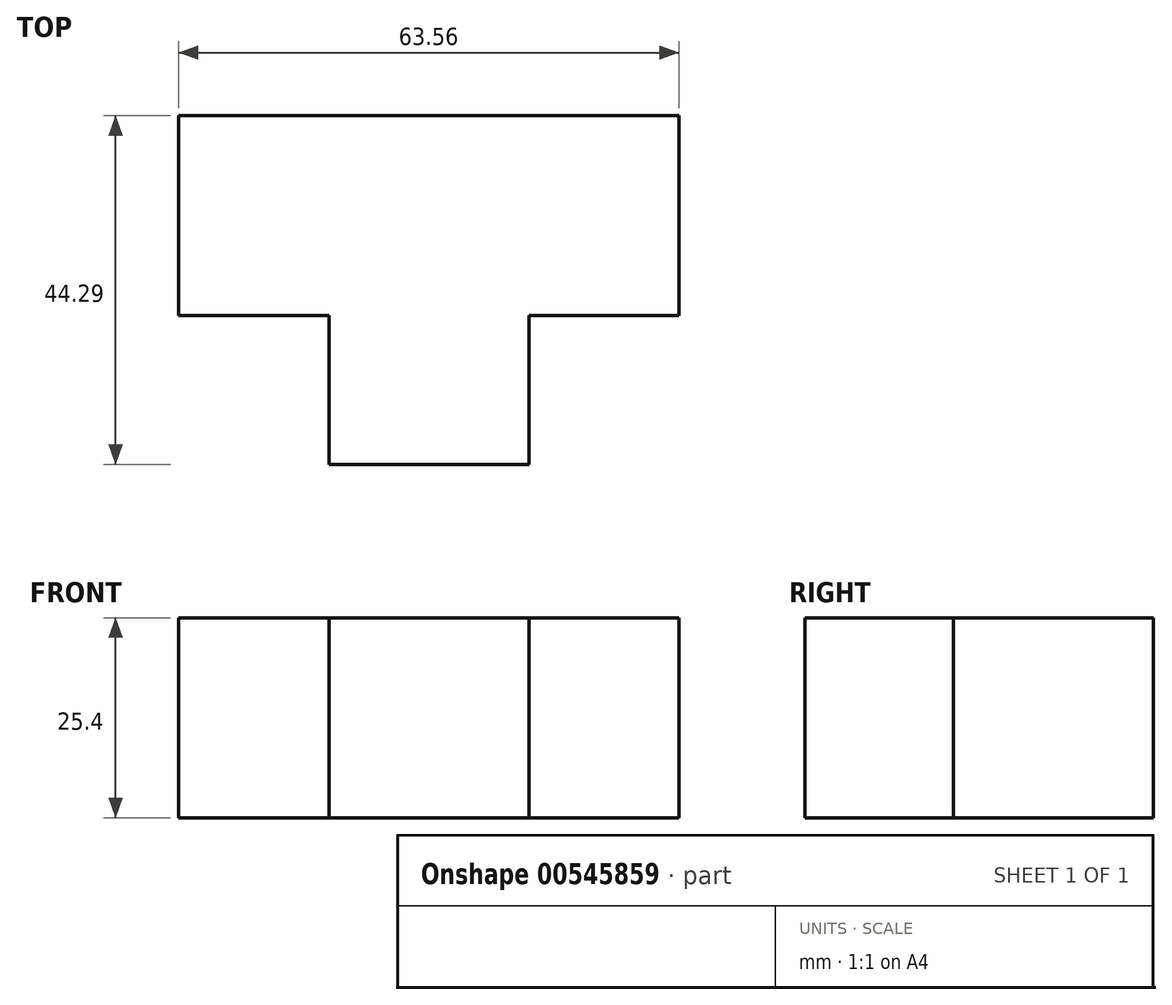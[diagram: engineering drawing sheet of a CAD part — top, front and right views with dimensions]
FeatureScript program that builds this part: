
annotation { "Feature Type Name" : "Feature", "Feature Type Description" : "" }
export const myFeature = defineFeature(function(context is Context, id is Id, definition is map)
    precondition{}
    {
        {
            var Q0;
            Q0=qCreatedBy(makeId("Top.planeOp"),FACE);
            var sketch = newSketch(context, id + "F0", { "sketchPlane" : qUnion([Q0])});
            skLineSegment(sketch, "E0", {"start": v(-61.18, 51.9) * mm, "end": v(2.38, 51.9) * mm});
            skLineSegment(sketch, "E1", {"start": v(2.38, 51.9) * mm, "end": v(2.38, 26.5) * mm});
            skLineSegment(sketch, "E2", {"start": v(2.38, 26.5) * mm, "end": v(-16.7, 26.5) * mm});
            skLineSegment(sketch, "E3", {"start": v(-16.7, 26.5) * mm, "end": v(-16.7, 7.62) * mm});
            skLineSegment(sketch, "E4", {"start": v(-16.7, 7.62) * mm, "end": v(-42.1, 7.62) * mm});
            skLineSegment(sketch, "E5", {"start": v(-42.1, 7.62) * mm, "end": v(-42.1, 26.5) * mm});
            skLineSegment(sketch, "E6", {"start": v(-42.1, 26.5) * mm, "end": v(-61.18, 26.5) * mm});
            skLineSegment(sketch, "E7", {"start": v(-61.18, 26.5) * mm, "end": v(-61.18, 51.9) * mm});
            skSolve(sketch);
        }
        {
            var Q0;
            Q0 = qSketchRegion(id + "F0", true);
            extrude(context, id + "F1", {"entities" : qUnion([Q0]), "depth" : 25.4 * mm, "offsetDistance" : 25.4 * mm});
        }
    });
